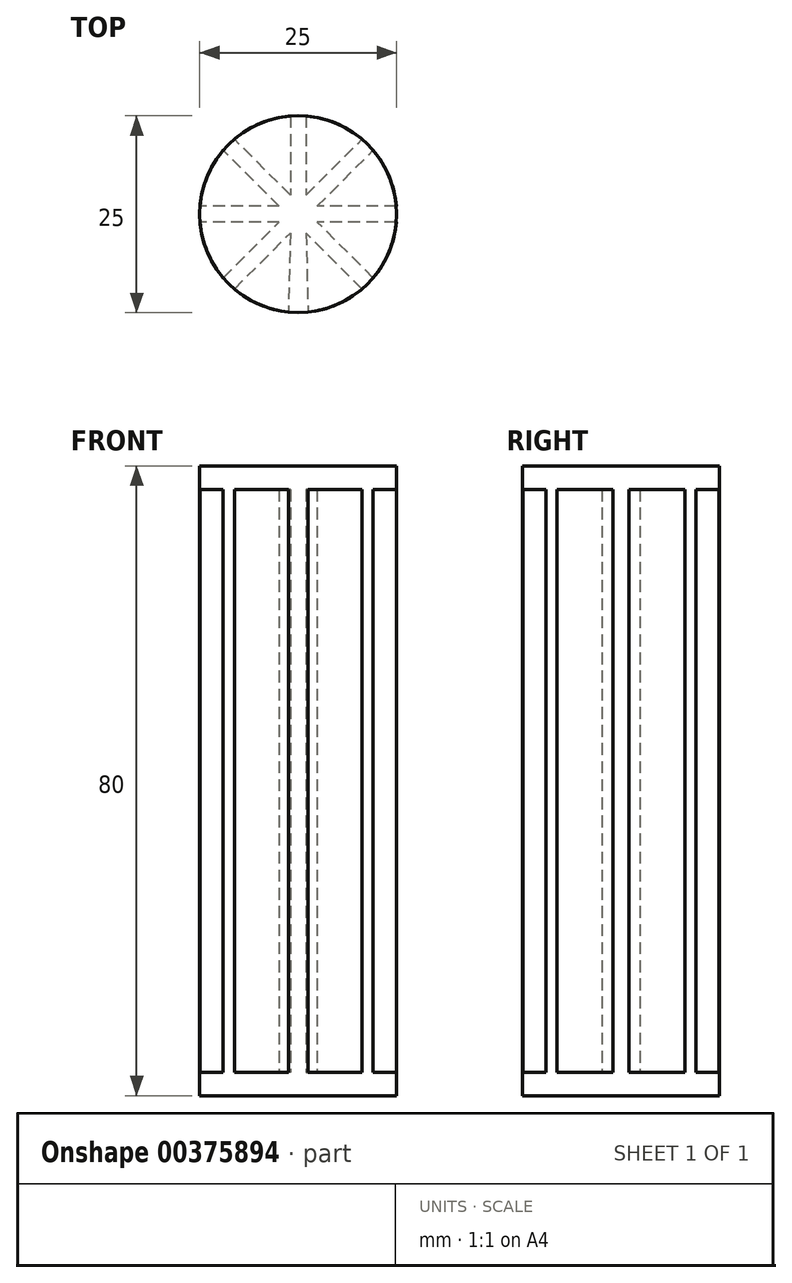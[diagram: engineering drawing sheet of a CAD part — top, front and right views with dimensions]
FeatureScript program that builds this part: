
annotation { "Feature Type Name" : "Feature", "Feature Type Description" : "" }
export const myFeature = defineFeature(function(context is Context, id is Id, definition is map)
    precondition{}
    {
        {
            var Q0;
            Q0=qCreatedBy(makeId("Top.planeOp"),FACE);
            var sketch = newSketch(context, id + "F0", { "sketchPlane" : qUnion([Q0])});
            skCircle(sketch, "E0", {"center": v(0, 0) * mm, "radius": 12.5 * mm});
            skLineSegment(sketch, "E1", {"start": v(0, 12.5) * mm, "end": v(0, -12.5) * mm, "construction": true});
            skLineSegment(sketch, "E2", {"start": v(-12.5, 0) * mm, "end": v(12.5, 0) * mm, "construction": true});
            skLineSegment(sketch, "E3", {"start": v(1, 12.46) * mm, "end": v(1, 2.41) * mm});
            skLineSegment(sketch, "E4.MirrorCS", {"start": v(-1, 12.46) * mm, "end": v(-1, 2.41) * mm});
            skLineSegment(sketch, "E5", {"start": v(12.46, -1) * mm, "end": v(2.41, -1) * mm});
            skLineSegment(sketch, "E6.MirrorCS", {"start": v(12.46, 1) * mm, "end": v(2.41, 1) * mm});
            skLineSegment(sketch, "E7", {"start": v(8.84, -8.84) * mm, "end": v(-8.84, 8.84) * mm, "construction": true});
            skLineSegment(sketch, "E8", {"start": v(-8.84, -8.84) * mm, "end": v(8.84, 8.84) * mm, "construction": true});
            skLineSegment(sketch, "E9", {"start": v(-8.1, -9.52) * mm, "end": v(0, -1.41) * mm});
            skLineSegment(sketch, "E10", {"start": v(9.52, -8.1) * mm, "end": v(1.41, 0) * mm});
            skLineSegment(sketch, "E11.MirrorCS", {"start": v(-9.52, -8.1) * mm, "end": v(-2.41, -1) * mm});
            skLineSegment(sketch, "E12.MirrorCS", {"start": v(8.1, -9.52) * mm, "end": v(-9.52, 8.1) * mm});
            skLineSegment(sketch, "E13.trimOffspring", {"start": v(-2.41, 1) * mm, "end": v(-12.46, 1) * mm});
            skLineSegment(sketch, "E14.trimOffspring", {"start": v(0, 1.41) * mm, "end": v(-8.1, 9.52) * mm});
            skLineSegment(sketch, "E15.trimOffspring", {"start": v(1, -2.41) * mm, "end": v(1.25, -12.44) * mm});
            skLineSegment(sketch, "E16.trimOffspring", {"start": v(1.41, 0) * mm, "end": v(9.52, 8.1) * mm});
            skLineSegment(sketch, "E17.trimOffspring", {"start": v(0, 1.41) * mm, "end": v(8.1, 9.52) * mm});
            skLineSegment(sketch, "E18.trimOffspring", {"start": v(-2.41, -1) * mm, "end": v(-12.46, -1) * mm});
            skLineSegment(sketch, "E19.trimOffspring", {"start": v(-1, -2.41) * mm, "end": v(-1.25, -12.44) * mm});
            skSolve(sketch);
        }
        {
            var Q0;
            {var subQ0=sQuery(id+"F0.wireOp",EDGE,"E3");var subQ1=sQuery(id+"F0.wireOp",EDGE,"E0");var subQ2=makeQuery(id+"F0.imprint","INTERSECT",VERTEX,{"disambiguationData":[OD(0.0)],"derivedFrom":[subQ1,subQ0]});Q0=makeQuery(id+"F0.imprint","IMPRINT",FACE,{"disambiguationData":[TD([[makeQuery(id+"F0.imprint","IMPRINT",EDGE,{"disambiguationData":[TD([[subQ2,1.0]])],"derivedFrom":subQ1}),1.0]])]});}
            var Q1;
            {var subQ0=sQuery(id+"F0.wireOp",EDGE,"E4.MirrorCS");var subQ1=sQuery(id+"F0.wireOp",EDGE,"E0");var subQ2=makeQuery(id+"F0.imprint","INTERSECT",VERTEX,{"disambiguationData":[OD(0.0)],"derivedFrom":[subQ1,subQ0]});Q1=makeQuery(id+"F0.imprint","IMPRINT",FACE,{"disambiguationData":[TD([[makeQuery(id+"F0.imprint","IMPRINT",EDGE,{"disambiguationData":[TD([[subQ2,-1.0]])],"derivedFrom":subQ1}),1.0]])]});}
            var Q2;
            {var subQ0=sQuery(id+"F0.wireOp",EDGE,"E6.MirrorCS");var subQ1=sQuery(id+"F0.wireOp",EDGE,"E0");var subQ2=makeQuery(id+"F0.imprint","INTERSECT",VERTEX,{"disambiguationData":[OD(0.0)],"derivedFrom":[subQ1,subQ0]});Q2=makeQuery(id+"F0.imprint","IMPRINT",FACE,{"disambiguationData":[TD([[makeQuery(id+"F0.imprint","IMPRINT",EDGE,{"disambiguationData":[TD([[subQ2,-1.0]])],"derivedFrom":subQ1}),1.0]])]});}
            var Q3;
            {var subQ0=sQuery(id+"F0.wireOp",EDGE,"E5");var subQ1=sQuery(id+"F0.wireOp",EDGE,"E0");var subQ2=makeQuery(id+"F0.imprint","INTERSECT",VERTEX,{"disambiguationData":[OD(0.0)],"derivedFrom":[subQ1,subQ0]});Q3=makeQuery(id+"F0.imprint","IMPRINT",FACE,{"disambiguationData":[TD([[makeQuery(id+"F0.imprint","IMPRINT",EDGE,{"disambiguationData":[TD([[subQ2,1.0]])],"derivedFrom":subQ1}),1.0]])]});}
            var Q4;
            {var subQ3=sQuery(id+"F0.wireOp",EDGE,"E13.trimOffspring");Q4=makeQuery(id+"F0.imprint","IMPRINT",FACE,{"disambiguationData":[TD([[makeQuery(id+"F0.imprint","IMPRINT",EDGE,{"derivedFrom":subQ3}),-1.0]])]});}
            var Q5;
            {var subQ0=sQuery(id+"F0.wireOp",EDGE,"E11.MirrorCS");Q5=makeQuery(id+"F0.imprint","IMPRINT",FACE,{"disambiguationData":[TD([[makeQuery(id+"F0.imprint","IMPRINT",EDGE,{"derivedFrom":subQ0}),1.0]])]});}
            var Q6;
            {var subQ3=sQuery(id+"F0.wireOp",EDGE,"E19.trimOffspring");Q6=makeQuery(id+"F0.imprint","IMPRINT",FACE,{"disambiguationData":[TD([[makeQuery(id+"F0.imprint","IMPRINT",EDGE,{"derivedFrom":subQ3}),-1.0]])]});}
            var Q7;
            {var subQ3=sQuery(id+"F0.wireOp",EDGE,"E15.trimOffspring");Q7=makeQuery(id+"F0.imprint","IMPRINT",FACE,{"disambiguationData":[TD([[makeQuery(id+"F0.imprint","IMPRINT",EDGE,{"derivedFrom":subQ3}),1.0]])]});}
            extrude(context, id + "F1", {"entities" : qUnion([Q0, Q1, Q2, Q3, Q4, Q5, Q6, Q7]), "depth" : 3 * mm});
        }
        {
            var Q0;
            {var subQ0=sQuery(id+"F0.wireOp",EDGE,"E3");var subQ1=sQuery(id+"F0.wireOp",EDGE,"E0");var subQ2=makeQuery(id+"F0.imprint","INTERSECT",VERTEX,{"disambiguationData":[OD(0.0)],"derivedFrom":[subQ1,subQ0]});Q0=makeQuery(id+"F0.imprint","IMPRINT",FACE,{"disambiguationData":[TD([[makeQuery(id+"F0.imprint","IMPRINT",EDGE,{"disambiguationData":[TD([[subQ2,-1.0]])],"derivedFrom":subQ1}),1.0]])]});}
            var Q1;
            {var subQ5=sQuery(id+"F0.wireOp",EDGE,"E0");var subQ14=sQuery(id+"F0.wireOp",EDGE,"E16.trimOffspring");var subQ16=makeQuery(id+"F0.imprint","INTERSECT",VERTEX,{"derivedFrom":[subQ5,subQ14]});Q1=makeQuery(id+"F0.imprint","IMPRINT",FACE,{"disambiguationData":[TD([[makeQuery(id+"F0.imprint","IMPRINT",EDGE,{"disambiguationData":[TD([[subQ16,-1.0]])],"derivedFrom":subQ5}),1.0]])]});}
            var Q2;
            {var subQ6=sQuery(id+"F0.wireOp",EDGE,"E11.MirrorCS");Q2=makeQuery(id+"F0.imprint","IMPRINT",FACE,{"disambiguationData":[TD([[makeQuery(id+"F0.imprint","IMPRINT",EDGE,{"derivedFrom":subQ6}),-1.0]])]});}
            var Q3;
            {var subQ2=sQuery(id+"F0.wireOp",EDGE,"E5");Q3=makeQuery(id+"F0.imprint","IMPRINT",FACE,{"disambiguationData":[TD([[makeQuery(id+"F0.imprint","IMPRINT",EDGE,{"derivedFrom":subQ2}),-1.0]])]});}
            var Q4;
            {var subQ0=sQuery(id+"F0.wireOp",EDGE,"E15.trimOffspring");Q4=makeQuery(id+"F0.imprint","IMPRINT",FACE,{"disambiguationData":[TD([[makeQuery(id+"F0.imprint","IMPRINT",EDGE,{"derivedFrom":subQ0}),-1.0]])]});}
            extrude(context, id + "F2", {"entities" : qUnion([Q0, Q1, Q2, Q3, Q4]), "operationType" : NewBodyOperationType.ADD, "depth" : 80 * mm});
        }
        {
            var Q0;
            Q0=makeQuery(id+"F2.opExtrude","CAP_FACE",FACE,{"disambiguationData":[OSD([sQuery(id+"F0.wireOp",EDGE,"E0"),sQuery(id+"F0.wireOp",EDGE,"E3"),sQuery(id+"F0.wireOp",EDGE,"E4.MirrorCS"),sQuery(id+"F0.wireOp",EDGE,"E5"),sQuery(id+"F0.wireOp",EDGE,"E6.MirrorCS")])],"isStart":false});
            var sketch = newSketch(context, id + "F3", { "sketchPlane" : qUnion([Q0])});
            skCircle(sketch, "E20.0", {"center": v(0, 0) * mm, "radius": 12.5 * mm});
            skSolve(sketch);
        }
        {
            var Q0;
            {var subQ1=sQuery(id+"F0.wireOp",EDGE,"E3");var subQ2=sQuery(id+"F0.wireOp",EDGE,"E0");var subQ5=makeQuery(id+"F2.opExtrude","CAP_EDGE",EDGE,{"disambiguationData":[OSD([subQ1]),TDD([makeQuery(id+"F0.imprint","IMPRINT",EDGE,{"disambiguationData":[TD([[makeQuery(id+"F0.imprint","INTERSECT",VERTEX,{"disambiguationData":[OD(0.0)],"derivedFrom":[subQ2,subQ1]}),-1.0]])],"derivedFrom":subQ1})])],"isStart":false});Q0=makeQuery(id+"F3.imprint","IMPRINT",FACE,{"disambiguationData":[TD([[makeQuery(id+"F3.imprint","IMPRINT",EDGE,{"derivedFrom":subQ5}),1.0]])]});}
            var Q1;
            {var subQ1=sQuery(id+"F0.wireOp",EDGE,"E3");var subQ2=sQuery(id+"F0.wireOp",EDGE,"E0");var subQ5=makeQuery(id+"F2.opExtrude","CAP_EDGE",EDGE,{"disambiguationData":[OSD([subQ1]),TDD([makeQuery(id+"F0.imprint","IMPRINT",EDGE,{"disambiguationData":[TD([[makeQuery(id+"F0.imprint","INTERSECT",VERTEX,{"disambiguationData":[OD(1.0)],"derivedFrom":[subQ2,subQ1]}),1.0]])],"derivedFrom":subQ1})])],"isStart":false});Q1=makeQuery(id+"F3.imprint","IMPRINT",FACE,{"disambiguationData":[TD([[makeQuery(id+"F3.imprint","IMPRINT",EDGE,{"derivedFrom":subQ5}),1.0]])]});}
            var Q2;
            {var subQ1=sQuery(id+"F0.wireOp",EDGE,"E4.MirrorCS");var subQ2=sQuery(id+"F0.wireOp",EDGE,"E0");var subQ5=makeQuery(id+"F2.opExtrude","CAP_EDGE",EDGE,{"disambiguationData":[OSD([subQ1]),TDD([makeQuery(id+"F0.imprint","IMPRINT",EDGE,{"disambiguationData":[TD([[makeQuery(id+"F0.imprint","INTERSECT",VERTEX,{"disambiguationData":[OD(1.0)],"derivedFrom":[subQ2,subQ1]}),1.0]])],"derivedFrom":subQ1})])],"isStart":false});Q2=makeQuery(id+"F3.imprint","IMPRINT",FACE,{"disambiguationData":[TD([[makeQuery(id+"F3.imprint","IMPRINT",EDGE,{"derivedFrom":subQ5}),-1.0]])]});}
            var Q3;
            {var subQ1=sQuery(id+"F0.wireOp",EDGE,"E4.MirrorCS");var subQ2=sQuery(id+"F0.wireOp",EDGE,"E0");var subQ5=makeQuery(id+"F2.opExtrude","CAP_EDGE",EDGE,{"disambiguationData":[OSD([subQ1]),TDD([makeQuery(id+"F0.imprint","IMPRINT",EDGE,{"disambiguationData":[TD([[makeQuery(id+"F0.imprint","INTERSECT",VERTEX,{"disambiguationData":[OD(0.0)],"derivedFrom":[subQ2,subQ1]}),-1.0]])],"derivedFrom":subQ1})])],"isStart":false});Q3=makeQuery(id+"F3.imprint","IMPRINT",FACE,{"disambiguationData":[TD([[makeQuery(id+"F3.imprint","IMPRINT",EDGE,{"derivedFrom":subQ5}),-1.0]])]});}
            var Q4;
            {var subQ1=sQuery(id+"F0.wireOp",EDGE,"E0");var subQ9=sQuery(id+"F0.wireOp",EDGE,"E3");var subQ13=makeQuery(id+"F2.opExtrude","CAP_EDGE",EDGE,{"disambiguationData":[OSD([subQ9]),TDD([makeQuery(id+"F0.imprint","IMPRINT",EDGE,{"disambiguationData":[TD([[makeQuery(id+"F0.imprint","INTERSECT",VERTEX,{"disambiguationData":[OD(0.0)],"derivedFrom":[subQ1,subQ9]}),-1.0]])],"derivedFrom":subQ9})])],"isStart":false});Q4=makeQuery(id+"F3.imprint","IMPRINT",FACE,{"disambiguationData":[TD([[makeQuery(id+"F3.imprint","IMPRINT",EDGE,{"derivedFrom":subQ13}),-1.0]])]});}
            var Q5;
            {var subQ2=sQuery(id+"F0.wireOp",EDGE,"E13.trimOffspring");var subQ4=makeQuery(id+"F2.opExtrude","CAP_EDGE",EDGE,{"disambiguationData":[OSD([subQ2])],"isStart":false});Q5=makeQuery(id+"F3.imprint","IMPRINT",FACE,{"disambiguationData":[TD([[makeQuery(id+"F3.imprint","IMPRINT",EDGE,{"derivedFrom":subQ4}),-1.0]])]});}
            var Q6;
            {var subQ1=makeQuery(id+"F2.opExtrude","CAP_EDGE",EDGE,{"disambiguationData":[OSD([sQuery(id+"F0.wireOp",EDGE,"E11.MirrorCS")])],"isStart":false});Q6=makeQuery(id+"F3.imprint","IMPRINT",FACE,{"disambiguationData":[TD([[makeQuery(id+"F3.imprint","IMPRINT",EDGE,{"derivedFrom":subQ1}),1.0]])]});}
            var Q7;
            {var subQ1=makeQuery(id+"F2.opExtrude","CAP_EDGE",EDGE,{"disambiguationData":[OSD([sQuery(id+"F0.wireOp",EDGE,"E9")])],"isStart":false});Q7=makeQuery(id+"F3.imprint","IMPRINT",FACE,{"disambiguationData":[TD([[makeQuery(id+"F3.imprint","IMPRINT",EDGE,{"derivedFrom":subQ1}),-1.0]])]});}
            var Q8;
            {var subQ2=sQuery(id+"F0.wireOp",EDGE,"E15.trimOffspring");var subQ4=makeQuery(id+"F2.opExtrude","CAP_EDGE",EDGE,{"disambiguationData":[OSD([subQ2])],"isStart":false});Q8=makeQuery(id+"F3.imprint","IMPRINT",FACE,{"disambiguationData":[TD([[makeQuery(id+"F3.imprint","IMPRINT",EDGE,{"derivedFrom":subQ4}),1.0]])]});}
            var Q9;
            {var subQ1=makeQuery(id+"F2.opExtrude","CAP_EDGE",EDGE,{"disambiguationData":[OSD([sQuery(id+"F0.wireOp",EDGE,"E5")])],"isStart":false});Q9=makeQuery(id+"F3.imprint","IMPRINT",FACE,{"disambiguationData":[TD([[makeQuery(id+"F3.imprint","IMPRINT",EDGE,{"derivedFrom":subQ1}),1.0]])]});}
            var Q10;
            {var subQ1=makeQuery(id+"F2.opExtrude","CAP_EDGE",EDGE,{"disambiguationData":[OSD([sQuery(id+"F0.wireOp",EDGE,"E6.MirrorCS")])],"isStart":false});Q10=makeQuery(id+"F3.imprint","IMPRINT",FACE,{"disambiguationData":[TD([[makeQuery(id+"F3.imprint","IMPRINT",EDGE,{"derivedFrom":subQ1}),-1.0]])]});}
            extrude(context, id + "F4", {"entities" : qUnion([Q0, Q1, Q2, Q3, Q4, Q5, Q6, Q7, Q8, Q9, Q10]), "operationType" : NewBodyOperationType.ADD, "oppositeDirection" : true, "depth" : 3 * mm});
        }
    });
